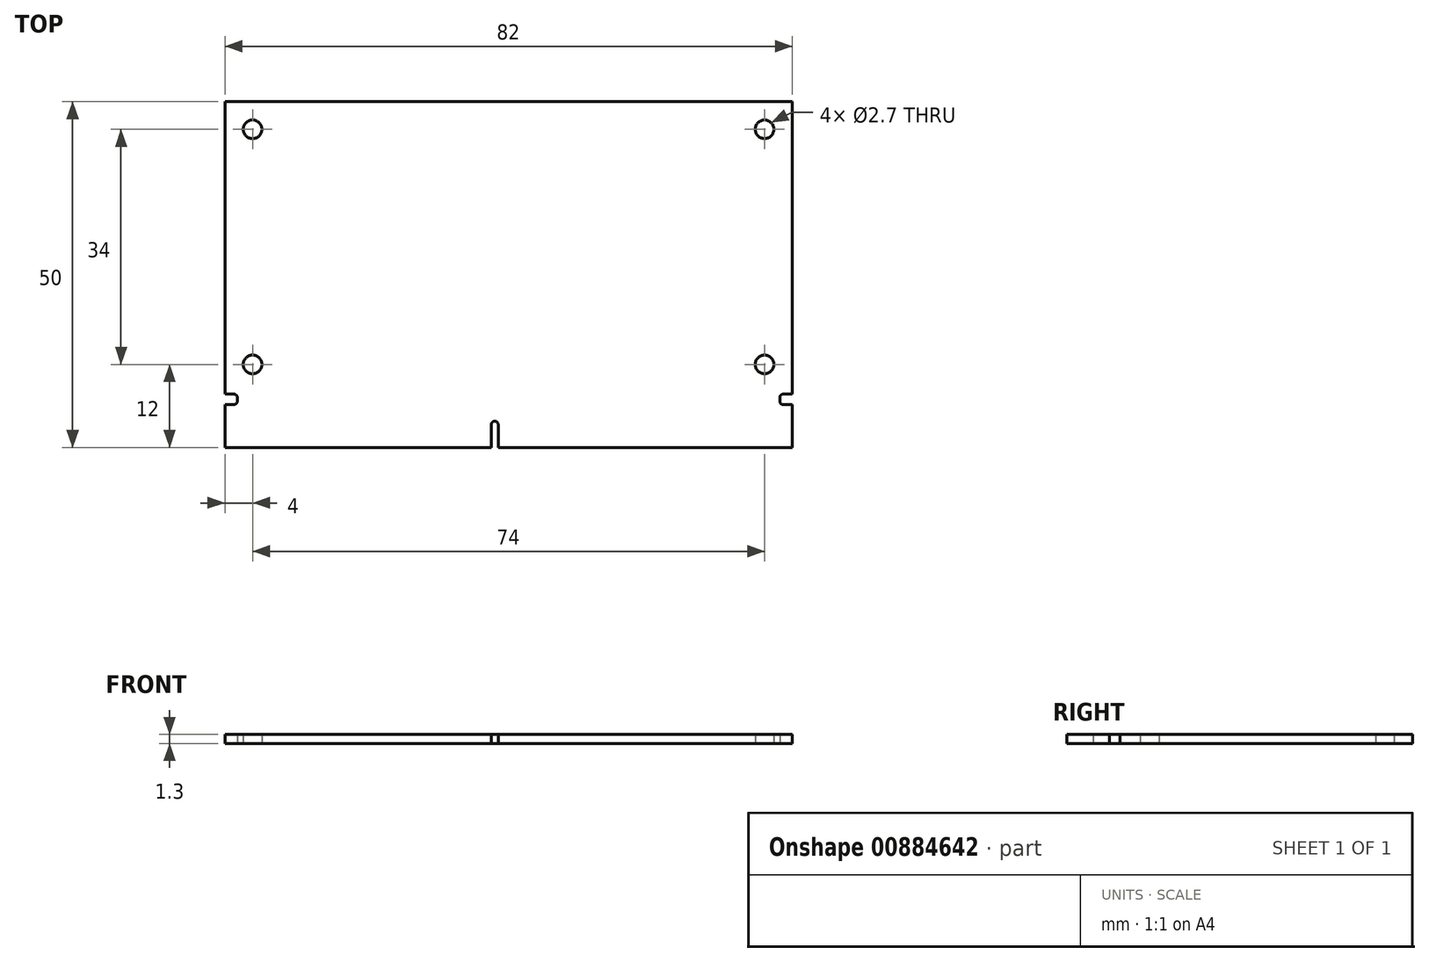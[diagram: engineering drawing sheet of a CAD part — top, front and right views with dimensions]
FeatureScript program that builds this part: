
annotation { "Feature Type Name" : "Feature", "Feature Type Description" : "" }
export const myFeature = defineFeature(function(context is Context, id is Id, definition is map)
    precondition{}
    {
        {
            var Q0;
            Q0=qCreatedBy(makeId("Top.planeOp"),FACE);
            var sketch = newSketch(context, id + "F0", { "sketchPlane" : qUnion([Q0])});
            skLineSegment(sketch, "E0.bottom", {"start": v(41, 25) * mm, "end": v(-41, 25) * mm});
            skPoint(sketch, "E0.middle", {"position": v(0, 0) * mm});
            skCircle(sketch, "E1", {"center": v(-37, 21) * mm, "radius": 1.35 * mm});
            skCircle(sketch, "E2", {"center": v(-37, 21) * mm, "radius": 3 * mm});
            skCircle(sketch, "E3.0.1.0", {"center": v(-37, -13) * mm, "radius": 3 * mm});
            skCircle(sketch, "E3.0.1.1", {"center": v(-37, -13) * mm, "radius": 1.35 * mm});
            skCircle(sketch, "E3.1.0.0", {"center": v(37, 21) * mm, "radius": 3 * mm});
            skCircle(sketch, "E3.1.0.1", {"center": v(37, 21) * mm, "radius": 1.35 * mm});
            skCircle(sketch, "E3.1.1.0", {"center": v(37, -13) * mm, "radius": 3 * mm});
            skCircle(sketch, "E3.1.1.1", {"center": v(37, -13) * mm, "radius": 1.35 * mm});
            skCircle(sketch, "E3.2.0.0", {"center": v(111, 21) * mm, "radius": 3 * mm});
            skCircle(sketch, "E3.2.0.1", {"center": v(111, 21) * mm, "radius": 1.35 * mm});
            skCircle(sketch, "E3.2.1.0", {"center": v(111, -13) * mm, "radius": 3 * mm});
            skCircle(sketch, "E3.2.1.1", {"center": v(111, -13) * mm, "radius": 1.35 * mm});
            skLineSegment(sketch, "E3.direction1", {"start": v(-37, 21) * mm, "end": v(37, 21) * mm, "construction": true});
            skLineSegment(sketch, "E3.direction2", {"start": v(-37, 21) * mm, "end": v(-37, -13) * mm, "construction": true});
            skLineSegment(sketch, "E4", {"start": v(-41, -25) * mm, "end": v(-2.5, -25) * mm});
            skLineSegment(sketch, "E5", {"start": v(-1.5, -25) * mm, "end": v(41, -25) * mm});
            skLineSegment(sketch, "E6", {"start": v(-2.5, -25) * mm, "end": v(-2.5, -21.7) * mm});
            skLineSegment(sketch, "E7", {"start": v(-1.5, -25) * mm, "end": v(-1.5, -21.7) * mm});
            skArc(sketch, "E8", {"start": v(-1.5, -21.7) * mm, "mid": v(-2, -21.2) * mm, "end": v(-2.5, -21.7) * mm});
            skLineSegment(sketch, "E9", {"start": v(-41, -25) * mm, "end": v(-41, -18.8) * mm});
            skLineSegment(sketch, "E10", {"start": v(-41, -18.8) * mm, "end": v(-39.7, -18.8) * mm});
            skLineSegment(sketch, "E11", {"start": v(-41, 25) * mm, "end": v(-41, -17.3) * mm});
            skLineSegment(sketch, "E12", {"start": v(-41, -17.3) * mm, "end": v(-39.7, -17.3) * mm});
            skLineSegment(sketch, "E13", {"start": v(-39.2, -17.8) * mm, "end": v(-39.2, -18.3) * mm});
            skPoint(sketch, "E14.visualSharp", {"position": v(-39.2, -17.3) * mm});
            skArc(sketch, "E14.filletArc", {"start": v(-39.2, -17.8) * mm, "mid": v(-39.35, -17.45) * mm, "end": v(-39.7, -17.3) * mm});
            skPoint(sketch, "E15.visualSharp", {"position": v(-39.2, -18.8) * mm});
            skArc(sketch, "E15.filletArc", {"start": v(-39.7, -18.8) * mm, "mid": v(-39.35, -18.65) * mm, "end": v(-39.2, -18.3) * mm});
            skLineSegment(sketch, "E16", {"start": v(0, 0) * mm, "end": v(0, -4.25) * mm, "construction": true});
            skLineSegment(sketch, "E17.MirrorCS", {"start": v(41, -18.8) * mm, "end": v(39.7, -18.8) * mm});
            skArc(sketch, "E18.MirrorCS", {"start": v(39.7, -18.8) * mm, "mid": v(39.35, -18.65) * mm, "end": v(39.2, -18.3) * mm});
            skArc(sketch, "E19.MirrorCS", {"start": v(39.2, -17.8) * mm, "mid": v(39.35, -17.45) * mm, "end": v(39.7, -17.3) * mm});
            skLineSegment(sketch, "E20.MirrorCS", {"start": v(41, -17.3) * mm, "end": v(39.7, -17.3) * mm});
            skLineSegment(sketch, "E21.MirrorCS", {"start": v(39.2, -17.8) * mm, "end": v(39.2, -18.3) * mm});
            skLineSegment(sketch, "E22", {"start": v(41, -25) * mm, "end": v(41, -18.8) * mm});
            skLineSegment(sketch, "E23", {"start": v(41, -17.3) * mm, "end": v(41, 25) * mm});
            skSolve(sketch);
        }
        {
            var Q0;
            Q0=makeQuery(id+"F0.imprint","IMPRINT",FACE,{"disambiguationData":[TD([[makeQuery(id+"F0.imprint","IMPRINT",EDGE,{"derivedFrom":sQuery(id+"F0.wireOp",EDGE,"E0.bottom")}),1.0]])]});
            var Q1;
            Q1=makeQuery(id+"F0.imprint","IMPRINT",FACE,{"disambiguationData":[TD([[makeQuery(id+"F0.imprint","IMPRINT",EDGE,{"derivedFrom":sQuery(id+"F0.wireOp",EDGE,"E3.0.1.0")}),1.0]])]});
            var Q2;
            Q2=makeQuery(id+"F0.imprint","IMPRINT",FACE,{"disambiguationData":[TD([[makeQuery(id+"F0.imprint","IMPRINT",EDGE,{"derivedFrom":sQuery(id+"F0.wireOp",EDGE,"E1")}),-1.0]])]});
            var Q3;
            Q3=makeQuery(id+"F0.imprint","IMPRINT",FACE,{"disambiguationData":[TD([[makeQuery(id+"F0.imprint","IMPRINT",EDGE,{"derivedFrom":sQuery(id+"F0.wireOp",EDGE,"E3.1.1.0")}),1.0]])]});
            var Q4;
            Q4=makeQuery(id+"F0.imprint","IMPRINT",FACE,{"disambiguationData":[TD([[makeQuery(id+"F0.imprint","IMPRINT",EDGE,{"derivedFrom":sQuery(id+"F0.wireOp",EDGE,"E3.1.0.0")}),1.0]])]});
            extrude(context, id + "F1", {"entities" : qUnion([Q0, Q1, Q2, Q3, Q4]), "depth" : 1.3 * mm, "offsetDistance" : 25 * mm});
        }
    });
